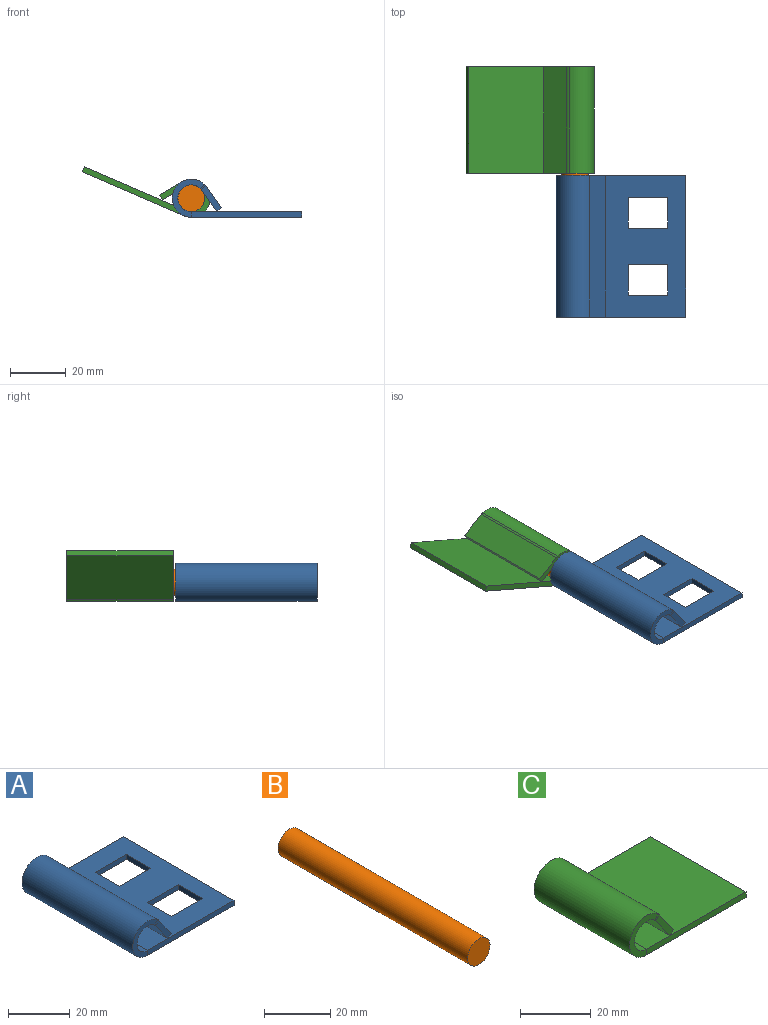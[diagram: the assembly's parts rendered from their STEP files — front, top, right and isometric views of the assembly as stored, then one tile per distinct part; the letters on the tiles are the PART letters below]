
ASSEMBLY  parts=3 mates=2
PART A: 26 faces, bbox 46.5x50.8x13.7 mm
  f0: plane 13.65x11.4mm, normal (0,1,0), area 45.2mm2, adj f2,f3,f10,f22
  f1: plane 13.65x11.4mm, normal (0,-1,0), area 45.2mm2, adj f2,f3,f11,f23
  f2: cylinder r=4.83mm len=50.8mm, axis (0,-1,0), area 950.1mm2, adj f0,f1,f15,f25
  f3: cylinder r=6.83mm len=50.8mm, axis (0,-1,0), area 1344mm2, adj f0,f1,f16,f24
  f4: plane 11.12x2mm, normal (-1,0,0), area 22.2mm2, adj f5,f14,f15,f16
  f5: plane 14.3x2mm, normal (0,1,0), area 28.6mm2, adj f4,f6,f15,f16
  f6: plane 11.12x2mm, normal (1,0,0), area 22.2mm2, adj f5,f14,f15,f16
  f7: plane 11.12x2mm, normal (-1,0,0), area 22.2mm2, adj f8,f13,f15,f16
  f8: plane 14.3x2mm, normal (0,1,0), area 28.6mm2, adj f7,f9,f15,f16
  f9: plane 11.12x2mm, normal (1,0,0), area 22.2mm2, adj f8,f13,f15,f16
  f10: plane 39.63x2mm, normal (0,1,0), area 79.3mm2, adj f0,f12,f15,f16
  f11: plane 39.63x2mm, normal (0,-1,0), area 79.3mm2, adj f1,f12,f15,f16
  f12: plane 50.8x2mm, normal (1,0,0), area 101.6mm2, adj f10,f11,f15,f16
  f13: plane 14.3x2mm, normal (0,-1,0), area 28.6mm2, adj f7,f9,f15,f16
  f14: plane 14.3x2mm, normal (0,-1,0), area 28.6mm2, adj f4,f6,f15,f16
  f15: plane 50.8x39.63mm, normal (0,0,1), area 1695.2mm2, adj f2,f4,f5,f6,f7,f8,f9,f10
  f16: plane 50.8x39.63mm, normal (0,0,-1), area 1695.2mm2, adj f3,f4,f5,f6,f7,f8,f9,f10
  f17: plane 9.07x7.28mm, normal (0,1,0), area 19.4mm2, adj f18,f20,f21,f22
  f18: plane 50.8x1.63mm, normal (0.58,0,-0.81), area 101.6mm2, adj f17,f19,f20,f21
  f19: plane 9.07x7.28mm, normal (0,-1,0), area 19.4mm2, adj f18,f20,f21,f23
  f20: plane 50.8x7.9mm, normal (-0.81,0,-0.58), area 493.7mm2, adj f17,f18,f19,f25
  f21: plane 50.8x7.9mm, normal (0.81,0,0.58), area 493.7mm2, adj f17,f18,f19,f24
  f22: plane 1.91x1.8mm, normal (0,1,0), area 1.3mm2, adj f0,f17,f24,f25
  f23: plane 1.91x1.8mm, normal (0,-1,0), area 1.3mm2, adj f1,f19,f24,f25
  f24: cylinder r=4mm len=50.8mm, axis (0,1,0), area 43.7mm2, adj f3,f21,f22,f23
  f25: cylinder r=2mm len=50.8mm, axis (0,1,0), area 21.9mm2, adj f2,f20,f22,f23
PART B: 3 faces, bbox 9.5x81x9.5 mm
  f0: cylinder r=4.76mm len=80.97mm, axis (0,1,0), area 2421.6mm2, adj f1,f2
  f1: plane 9.52x9.52mm, normal (0,-1,0), area 71.2mm2, adj f0
  f2: plane 9.52x9.52mm, normal (0,1,0), area 71.2mm2, adj f0
PART C: 18 faces, bbox 46.5x38.1x13.7 mm
  f0: plane 13.65x11.4mm, normal (0,1,0), area 45.2mm2, adj f2,f3,f4,f15
  f1: plane 13.65x11.4mm, normal (0,-1,0), area 45.2mm2, adj f2,f3,f6,f14
  f2: cylinder r=6.83mm len=38.1mm, axis (0,-1,0), area 1008mm2, adj f0,f1,f7,f16
  f3: cylinder r=4.83mm len=38.1mm, axis (0,-1,0), area 712.6mm2, adj f0,f1,f8,f17
  f4: plane 39.63x2mm, normal (0,1,0), area 79.3mm2, adj f0,f5,f7,f8
  f5: plane 38.1x2mm, normal (1,0,0), area 76.2mm2, adj f4,f6,f7,f8
  f6: plane 39.63x2mm, normal (0,-1,0), area 79.3mm2, adj f1,f5,f7,f8
  f7: plane 39.63x38.1mm, normal (0,0,-1), area 1509.9mm2, adj f2,f4,f5,f6
  f8: plane 39.63x38.1mm, normal (0,0,1), area 1509.9mm2, adj f3,f4,f5,f6
  f9: plane 9.07x7.28mm, normal (0,1,0), area 19.4mm2, adj f11,f12,f13,f15
  f10: plane 9.07x7.28mm, normal (0,-1,0), area 19.4mm2, adj f11,f12,f13,f14
  f11: plane 38.1x1.63mm, normal (0.58,0,-0.81), area 76.2mm2, adj f9,f10,f12,f13
  f12: plane 38.1x7.9mm, normal (0.81,0,0.58), area 370.3mm2, adj f9,f10,f11,f16
  f13: plane 38.1x7.9mm, normal (-0.81,0,-0.58), area 370.3mm2, adj f9,f10,f11,f17
  f14: plane 1.91x1.8mm, normal (0,-1,0), area 1.3mm2, adj f1,f10,f16,f17
  f15: plane 1.91x1.8mm, normal (0,1,0), area 1.3mm2, adj f0,f9,f16,f17
  f16: cylinder r=4mm len=38.1mm, axis (0,-1,0), area 32.8mm2, adj f2,f12,f14,f15
  f17: cylinder r=2mm len=38.1mm, axis (0,-1,0), area 16.4mm2, adj f3,f13,f14,f15
PLACE A t=(-4.65,23.64,-12.81)mm fixed
PLACE B t=(-4.65,62.61,37.14)mm
PLACE C rot(axis=(-0.2,0,-0.98),180deg) t=(154.04,24.51,-84.85)mm
MATE fastened B.f0 <-> A.f2  axis (0,1,0) through (-4.65,-18.36,-12.81)mm
MATE revolute C.f2 <-> B.f0  axis (0,1,0) through (-4.65,62.61,-12.81)mm
